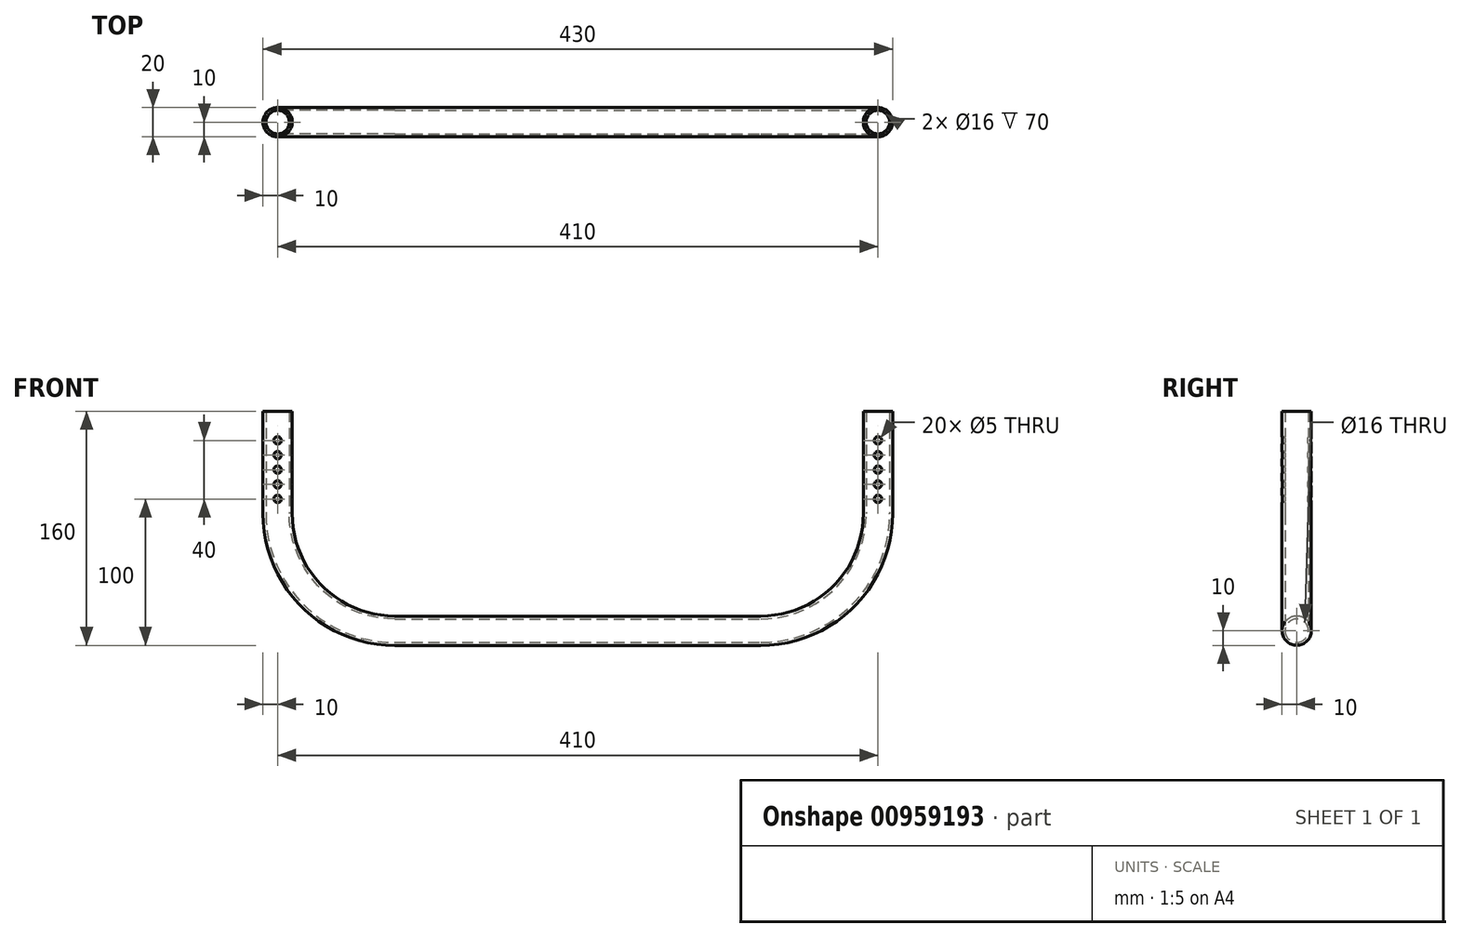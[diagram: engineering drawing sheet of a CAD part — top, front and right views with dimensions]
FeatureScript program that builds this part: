
annotation { "Feature Type Name" : "Feature", "Feature Type Description" : "" }
export const myFeature = defineFeature(function(context is Context, id is Id, definition is map)
    precondition{}
    {
        {
            var Q0;
            Q0=qCreatedBy(makeId("Front.planeOp"),FACE);
            var sketch = newSketch(context, id + "F0", { "sketchPlane" : qUnion([Q0])});
            skLineSegment(sketch, "E0", {"start": v(-205, 150) * mm, "end": v(-205, 80) * mm});
            skLineSegment(sketch, "E1", {"start": v(-125, 0) * mm, "end": v(0, 0) * mm});
            skLineSegment(sketch, "E2", {"start": v(0, 192.14) * mm, "end": v(0, -32.18) * mm, "construction": true});
            skPoint(sketch, "E3.visualSharp", {"position": v(-205, 0) * mm});
            skArc(sketch, "E3.filletArc", {"start": v(-205, 80) * mm, "mid": v(-181.57, 23.43) * mm, "end": v(-125, 0) * mm});
            skPoint(sketch, "E4.MirrorCS.end.orphan", {"position": v(0, 0) * mm});
            skCircle(sketch, "E5", {"center": v(-205, 90) * mm, "radius": 2.5 * mm});
            skCircle(sketch, "E6.0.1.0", {"center": v(-205, 100) * mm, "radius": 2.5 * mm});
            skCircle(sketch, "E6.0.2.0", {"center": v(-205, 110) * mm, "radius": 2.5 * mm});
            skCircle(sketch, "E6.0.3.0", {"center": v(-205, 120) * mm, "radius": 2.5 * mm});
            skCircle(sketch, "E6.0.4.0", {"center": v(-205, 130) * mm, "radius": 2.5 * mm});
            skLineSegment(sketch, "E6.direction1", {"start": v(-205, 90) * mm, "end": v(-180, 90) * mm, "construction": true});
            skLineSegment(sketch, "E6.direction2", {"start": v(-205, 90) * mm, "end": v(-205, 100) * mm, "construction": true});
            skSolve(sketch);
        }
        {
            var Q0;
            Q0=sQuery(id+"F0.wireOp",VERTEX,"E0.start");
            var Q1;
            Q1=sQuery(id+"F0.wireOp",EDGE,"E0");
            cPlane(context, id + "F1", {"entities" : qUnion([Q0, Q1]), "cplaneType" : CPlaneType.CURVE_POINT, "offset" : 25 * mm, "width" : 150 * mm, "height" : 150 * mm});
        }
        {
            var Q0;
            Q0=qCreatedBy(id+"F1.planeOp",FACE);
            var sketch = newSketch(context, id + "F2", { "sketchPlane" : qUnion([Q0])});
            skPoint(sketch, "E7.0", {"position": v(-205, 0) * mm});
            skCircle(sketch, "E8", {"center": v(-205, 0) * mm, "radius": 10 * mm});
            skCircle(sketch, "E9", {"center": v(-205, 0) * mm, "radius": 8 * mm});
            skSolve(sketch);
        }
        {
            var Q0;
            Q0=makeQuery(id+"F2.imprint","IMPRINT",FACE,{"disambiguationData":[TD([[makeQuery(id+"F2.imprint","IMPRINT",EDGE,{"derivedFrom":sQuery(id+"F2.wireOp",EDGE,"E8")}),1.0]])]});
            var Q1;
            Q1=sQuery(id+"F0.wireOp",EDGE,"E0");
            var Q2;
            Q2=sQuery(id+"F0.wireOp",EDGE,"E3.filletArc");
            var Q3;
            Q3=sQuery(id+"F0.wireOp",EDGE,"E1");
            var Q4;
            Q4=sQuery(id+"F0.wireOp",EDGE,"E4.MirrorCS");
            var Q5;
            Q5=sQuery(id+"F0.wireOp",EDGE,"660c7de8-432a-43e8-b99b-223396b1d9f50.MirrorCS");
            var Q6;
            Q6=sQuery(id+"F0.wireOp",EDGE,"df417fcc-0166-40a6-a6f3-f3e4604c36390.MirrorCS");
            sweep(context, id + "F3", {"profiles" : qUnion([Q0]), "path" : qUnion([Q1, Q2, Q3, Q4, Q5, Q6])});
        }
        {
            var Q0;
            Q0=qSketchRegion(id+"F0",true);
            extrude(context, id + "F4", {"entities" : qUnion([Q0]), "operationType" : NewBodyOperationType.REMOVE, "endBound" : BoundingType.SYMMETRIC, "oppositeDirection" : true, "depth" : 25 * mm, "offsetDistance" : 25 * mm});
        }
        {
            var Q0;
            Q0=makeQuery(id+"F3.opSweep","SWEPT_BODY",BODY,{"disambiguationData":[OSD([sQuery(id+"F0.wireOp",EDGE,"E1"),sQuery(id+"F2.wireOp",EDGE,"E8"),sQuery(id+"F2.wireOp",EDGE,"E9")])]});
            var Q1;
            Q1=makeQuery(id+"F3.opSweep","CAP_FACE",FACE,{"disambiguationData":[OSD([sQuery(id+"F0.wireOp",VERTEX,"E1.end"),sQuery(id+"F2.wireOp",EDGE,"E8"),sQuery(id+"F2.wireOp",EDGE,"E9")])],"isStart":false});
            mirror(context, id + "F5", {"operationType" : NewBodyOperationType.ADD, "entities" : qUnion([Q0]), "mirrorPlane" : qUnion([Q1])});
        }
    });
